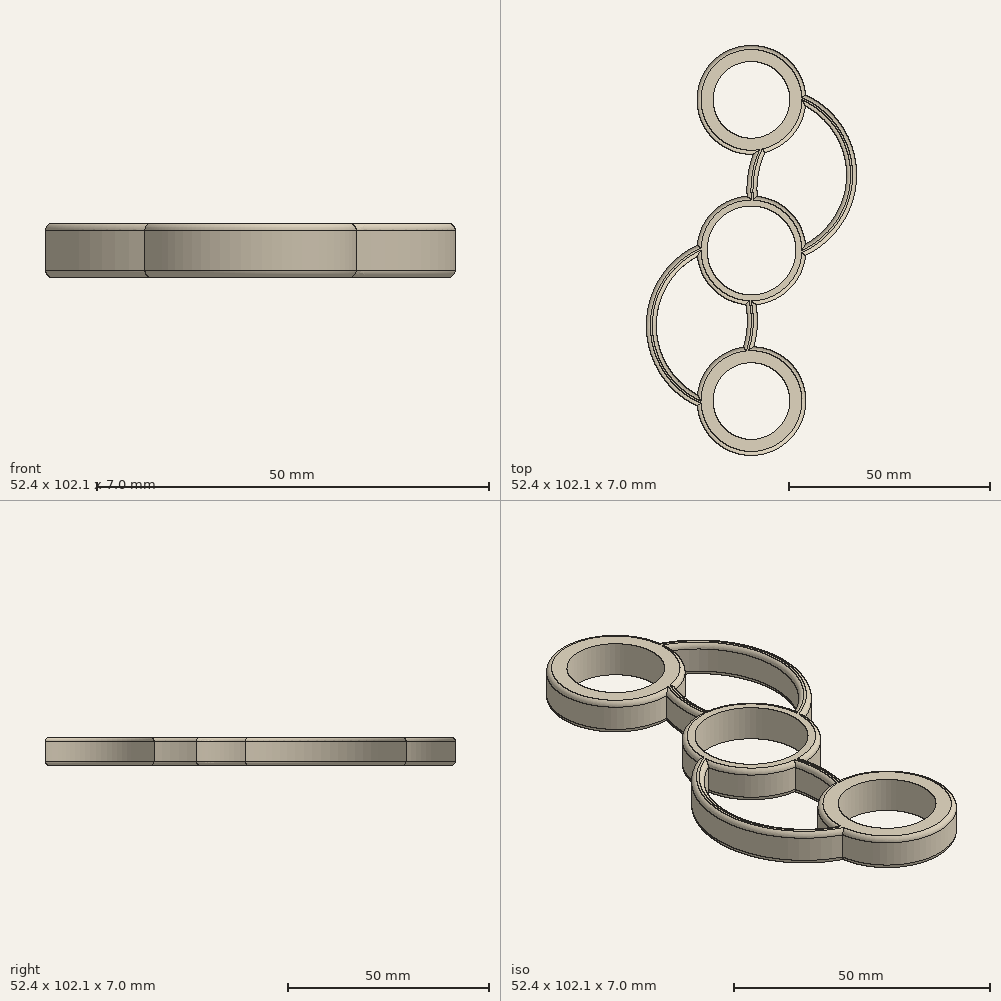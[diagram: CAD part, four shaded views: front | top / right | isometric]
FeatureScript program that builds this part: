
annotation { "Feature Type Name" : "Feature", "Feature Type Description" : "" }
export const myFeature = defineFeature(function(context is Context, id is Id, definition is map)
    precondition{}
    {
        {
            var Q0;
            Q0=qCreatedBy(makeId("Top.planeOp"),FACE);
            var sketch = newSketch(context, id + "F0", { "sketchPlane" : qUnion([Q0])});
            skCircle(sketch, "E0", {"center": v(0, 0) * mm, "radius": 11.05 * mm});
            skCircle(sketch, "E1", {"center": v(0, -37.5) * mm, "radius": 9.55 * mm});
            skCircle(sketch, "E2", {"center": v(0, 37.5) * mm, "radius": 9.55 * mm});
            skArc(sketch, "E3", {"start": v(3.4, 24.39) * mm, "mid": v(1.71, 19.06) * mm, "end": v(1.41, 13.48) * mm});
            skPoint(sketch, "E4.orphan", {"position": v(13.26, 34.7) * mm});
            skArc(sketch, "E5.trimOffspring", {"start": v(-2, -24.1) * mm, "mid": v(-1.06, -18.82) * mm, "end": v(-1.41, -13.48) * mm});
            skArc(sketch, "E6.0", {"start": v(0.51, 23.96) * mm, "mid": v(-0.86, 18.82) * mm, "end": v(-1.1, 13.5) * mm});
            skArc(sketch, "E7.0", {"start": v(0.63, -23.96) * mm, "mid": v(1.44, -18.76) * mm, "end": v(1.13, -13.5) * mm});
            skArc(sketch, "E8", {"start": v(-1.1, 13.5) * mm, "mid": v(-9.53, 9.64) * mm, "end": v(-13.5, 1.25) * mm});
            skArc(sketch, "E9.trimOffspring", {"start": v(1.13, -13.5) * mm, "mid": v(9.54, -9.62) * mm, "end": v(13.5, -1.25) * mm});
            skArc(sketch, "E10", {"start": v(3.4, 24.39) * mm, "mid": v(10.23, 28.61) * mm, "end": v(13.46, 35.96) * mm});
            skArc(sketch, "E11", {"start": v(-2, -24.1) * mm, "mid": v(-9.75, -28.09) * mm, "end": v(-13.46, -35.96) * mm});
            skLineSegment(sketch, "E12", {"start": v(0, -37.5) * mm, "end": v(-13.55, -37.5) * mm, "construction": true});
            skArc(sketch, "E13", {"start": v(-13.55, 0) * mm, "mid": v(-23.95, -18.75) * mm, "end": v(-13.55, -37.5) * mm, "construction": true});
            skLineSegment(sketch, "E14", {"start": v(0, 37.5) * mm, "end": v(13.55, 37.5) * mm, "construction": true});
            skLineSegment(sketch, "E15", {"start": v(0, 0) * mm, "end": v(16.47, 0) * mm, "construction": true});
            skArc(sketch, "E16", {"start": v(13.5, -1.25) * mm, "mid": v(26.19, 18.75) * mm, "end": v(13.5, 38.75) * mm});
            skArc(sketch, "E17.0", {"start": v(13.46, 1.54) * mm, "mid": v(23.69, 18.75) * mm, "end": v(13.46, 35.96) * mm});
            skArc(sketch, "E18.1.0", {"start": v(-13.5, 1.25) * mm, "mid": v(-26.19, -18.75) * mm, "end": v(-13.5, -38.75) * mm});
            skArc(sketch, "E18.1.1", {"start": v(-13.46, -1.54) * mm, "mid": v(-23.69, -18.75) * mm, "end": v(-13.46, -35.96) * mm});
            skArc(sketch, "E19.trimOffspring", {"start": v(13.5, 38.75) * mm, "mid": v(-10.18, 46.44) * mm, "end": v(0.51, 23.96) * mm});
            skArc(sketch, "E20.trimOffspring", {"start": v(13.46, 1.54) * mm, "mid": v(9.54, 9.63) * mm, "end": v(1.41, 13.48) * mm});
            skPoint(sketch, "E21.orphan", {"position": v(12.43, 1.01) * mm});
            skPoint(sketch, "E22.orphan", {"position": v(-12.43, -1.01) * mm});
            skArc(sketch, "E23.trimOffspring", {"start": v(-13.46, -1.54) * mm, "mid": v(-9.54, -9.63) * mm, "end": v(-1.41, -13.48) * mm});
            skPoint(sketch, "E24.orphan", {"position": v(-12.43, -36.49) * mm});
            skArc(sketch, "E25.trimOffspring", {"start": v(-13.5, -38.75) * mm, "mid": v(9.8, -46.86) * mm, "end": v(0.63, -23.96) * mm});
            skSolve(sketch);
        }
        {
            var Q0;
            Q0 = qSketchRegion(id + "F0", true);
            extrude(context, id + "F1", {"entities" : qUnion([Q0]), "depth" : 7 * mm, "offsetDistance" : 25 * mm});
        }
        {
            var Q0;
            Q0=makeQuery(id+"F1.opExtrude","CAP_EDGE",EDGE,{"disambiguationData":[OSD([sQuery(id+"F0.wireOp",EDGE,"x7SxP1iB-2Qy3-dVEY-MXrG-xvjEvFVd1tLw")])],"isStart":false});
            var Q1;
            Q1=makeQuery(id+"F1.opExtrude","CAP_EDGE",EDGE,{"disambiguationData":[OSD([sQuery(id+"F0.wireOp",EDGE,"x7SxP1iB-2Qy3-dVEY-MXrG-xvjEvFVd1tLw")])],"isStart":true});
            var Q2;
            Q2=makeQuery(id+"F1.opExtrude","CAP_EDGE",EDGE,{"disambiguationData":[OSD([sQuery(id+"F0.wireOp",EDGE,"a062c1e4-bb9d-4540-8efc-73d87e6f19ef.0")])],"isStart":false});
            var Q3;
            Q3=makeQuery(id+"F1.opExtrude","CAP_EDGE",EDGE,{"disambiguationData":[OSD([sQuery(id+"F0.wireOp",EDGE,"E7.0")])],"isStart":false});
            var Q4;
            Q4=makeQuery(id+"F1.opExtrude","CAP_EDGE",EDGE,{"disambiguationData":[OSD([sQuery(id+"F0.wireOp",EDGE,"E7.0")])],"isStart":true});
            var Q5;
            Q5=makeQuery(id+"F1.opExtrude","CAP_EDGE",EDGE,{"disambiguationData":[OSD([sQuery(id+"F0.wireOp",EDGE,"E5.trimOffspring")])],"isStart":false});
            var Q6;
            Q6=makeQuery(id+"F1.opExtrude","CAP_EDGE",EDGE,{"disambiguationData":[OSD([sQuery(id+"F0.wireOp",EDGE,"E5.trimOffspring")])],"isStart":true});
            var Q7;
            Q7=makeQuery(id+"F1.opExtrude","CAP_EDGE",EDGE,{"disambiguationData":[OSD([sQuery(id+"F0.wireOp",EDGE,"laMGJ9zr-upjW-nV1x-AArC-vHo1Xi3B8won")])],"isStart":false});
            var Q8;
            Q8=makeQuery(id+"F1.opExtrude","CAP_EDGE",EDGE,{"disambiguationData":[OSD([sQuery(id+"F0.wireOp",EDGE,"4f1ea1fe-4552-4784-b4ea-b08223bb9b54.0")])],"isStart":false});
            var Q9;
            Q9=makeQuery(id+"F1.opExtrude","CAP_EDGE",EDGE,{"disambiguationData":[OSD([sQuery(id+"F0.wireOp",EDGE,"E6.0")])],"isStart":false});
            var Q10;
            Q10=makeQuery(id+"F1.opExtrude","CAP_EDGE",EDGE,{"disambiguationData":[OSD([sQuery(id+"F0.wireOp",EDGE,"E3")])],"isStart":false});
            var Q11;
            Q11=makeQuery(id+"F1.opExtrude","CAP_EDGE",EDGE,{"disambiguationData":[OSD([sQuery(id+"F0.wireOp",EDGE,"E3")])],"isStart":true});
            var Q12;
            Q12=makeQuery(id+"F1.opExtrude","CAP_EDGE",EDGE,{"disambiguationData":[OSD([sQuery(id+"F0.wireOp",EDGE,"E6.0")])],"isStart":true});
            var Q13;
            Q13=makeQuery(id+"F1.opExtrude","CAP_EDGE",EDGE,{"disambiguationData":[OSD([sQuery(id+"F0.wireOp",EDGE,"4f1ea1fe-4552-4784-b4ea-b08223bb9b54.0")])],"isStart":true});
            var Q14;
            Q14=makeQuery(id+"F1.opExtrude","CAP_EDGE",EDGE,{"disambiguationData":[OSD([sQuery(id+"F0.wireOp",EDGE,"laMGJ9zr-upjW-nV1x-AArC-vHo1Xi3B8won")])],"isStart":true});
            var Q15;
            Q15=makeQuery(id+"F1.opExtrude","CAP_EDGE",EDGE,{"disambiguationData":[OSD([sQuery(id+"F0.wireOp",EDGE,"E18.1.0")])],"isStart":false});
            var Q16;
            Q16=makeQuery(id+"F1.opExtrude","CAP_EDGE",EDGE,{"disambiguationData":[OSD([sQuery(id+"F0.wireOp",EDGE,"E18.1.1")])],"isStart":false});
            var Q17;
            Q17=makeQuery(id+"F1.opExtrude","CAP_EDGE",EDGE,{"disambiguationData":[OSD([sQuery(id+"F0.wireOp",EDGE,"E16")])],"isStart":false});
            var Q18;
            Q18=makeQuery(id+"F1.opExtrude","CAP_EDGE",EDGE,{"disambiguationData":[OSD([sQuery(id+"F0.wireOp",EDGE,"E17.0")])],"isStart":false});
            var Q19;
            Q19=makeQuery(id+"F1.opExtrude","CAP_EDGE",EDGE,{"disambiguationData":[OSD([sQuery(id+"F0.wireOp",EDGE,"E10")])],"isStart":false});
            var Q20;
            Q20=makeQuery(id+"F1.opExtrude","CAP_EDGE",EDGE,{"disambiguationData":[OSD([sQuery(id+"F0.wireOp",EDGE,"E19.trimOffspring")])],"isStart":false});
            var Q21;
            Q21=makeQuery(id+"F1.opExtrude","CAP_EDGE",EDGE,{"disambiguationData":[OSD([sQuery(id+"F0.wireOp",EDGE,"E20.trimOffspring")])],"isStart":false});
            var Q22;
            Q22=makeQuery(id+"F1.opExtrude","CAP_EDGE",EDGE,{"disambiguationData":[OSD([sQuery(id+"F0.wireOp",EDGE,"E8")])],"isStart":false});
            var Q23;
            Q23=makeQuery(id+"F1.opExtrude","CAP_EDGE",EDGE,{"disambiguationData":[OSD([sQuery(id+"F0.wireOp",EDGE,"E23.trimOffspring")])],"isStart":false});
            var Q24;
            Q24=makeQuery(id+"F1.opExtrude","CAP_EDGE",EDGE,{"disambiguationData":[OSD([sQuery(id+"F0.wireOp",EDGE,"E9.trimOffspring")])],"isStart":false});
            var Q25;
            Q25=makeQuery(id+"F1.opExtrude","CAP_EDGE",EDGE,{"disambiguationData":[OSD([sQuery(id+"F0.wireOp",EDGE,"E25.trimOffspring")])],"isStart":false});
            var Q26;
            Q26=makeQuery(id+"F1.opExtrude","CAP_EDGE",EDGE,{"disambiguationData":[OSD([sQuery(id+"F0.wireOp",EDGE,"E11")])],"isStart":false});
            var Q27;
            Q27=makeQuery(id+"F1.opExtrude","CAP_EDGE",EDGE,{"disambiguationData":[OSD([sQuery(id+"F0.wireOp",EDGE,"E19.trimOffspring")])],"isStart":true});
            var Q28;
            Q28=makeQuery(id+"F1.opExtrude","CAP_EDGE",EDGE,{"disambiguationData":[OSD([sQuery(id+"F0.wireOp",EDGE,"E10")])],"isStart":true});
            var Q29;
            Q29=makeQuery(id+"F1.opExtrude","CAP_EDGE",EDGE,{"disambiguationData":[OSD([sQuery(id+"F0.wireOp",EDGE,"E16")])],"isStart":true});
            var Q30;
            Q30=makeQuery(id+"F1.opExtrude","CAP_EDGE",EDGE,{"disambiguationData":[OSD([sQuery(id+"F0.wireOp",EDGE,"E17.0")])],"isStart":true});
            var Q31;
            Q31=makeQuery(id+"F1.opExtrude","CAP_EDGE",EDGE,{"disambiguationData":[OSD([sQuery(id+"F0.wireOp",EDGE,"E25.trimOffspring")])],"isStart":true});
            var Q32;
            Q32=makeQuery(id+"F1.opExtrude","CAP_EDGE",EDGE,{"disambiguationData":[OSD([sQuery(id+"F0.wireOp",EDGE,"E11")])],"isStart":true});
            var Q33;
            Q33=makeQuery(id+"F1.opExtrude","CAP_EDGE",EDGE,{"disambiguationData":[OSD([sQuery(id+"F0.wireOp",EDGE,"E9.trimOffspring")])],"isStart":true});
            var Q34;
            Q34=makeQuery(id+"F1.opExtrude","CAP_EDGE",EDGE,{"disambiguationData":[OSD([sQuery(id+"F0.wireOp",EDGE,"E20.trimOffspring")])],"isStart":true});
            var Q35;
            Q35=makeQuery(id+"F1.opExtrude","CAP_EDGE",EDGE,{"disambiguationData":[OSD([sQuery(id+"F0.wireOp",EDGE,"E8")])],"isStart":true});
            var Q36;
            Q36=makeQuery(id+"F1.opExtrude","CAP_EDGE",EDGE,{"disambiguationData":[OSD([sQuery(id+"F0.wireOp",EDGE,"E23.trimOffspring")])],"isStart":true});
            var Q37;
            Q37=makeQuery(id+"F1.opExtrude","CAP_EDGE",EDGE,{"disambiguationData":[OSD([sQuery(id+"F0.wireOp",EDGE,"E18.1.0")])],"isStart":true});
            fillet(context, id + "F2", {"entities" : qUnion([Q0, Q1, Q2, Q3, Q4, Q5, Q6, Q7, Q8, Q9, Q10, Q11, Q12, Q13, Q14, Q15, Q16, Q17, Q18, Q19, Q20, Q21, Q22, Q23, Q24, Q25, Q26, Q27, Q28, Q29, Q30, Q31, Q32, Q33, Q34, Q35, Q36, Q37]), "radius" : 1 * mm, "tangentPropagation" : true, "allowEdgeOverflow" : false});
        }
    });
